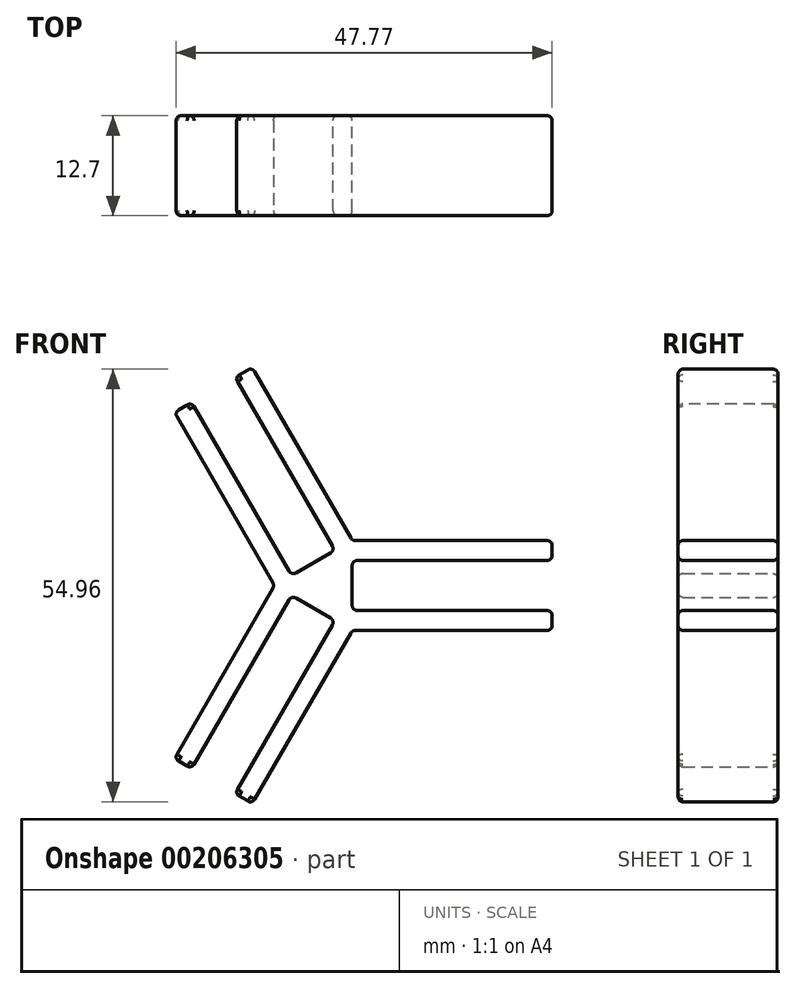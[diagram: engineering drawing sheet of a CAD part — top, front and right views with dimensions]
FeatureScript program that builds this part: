
annotation { "Feature Type Name" : "Feature", "Feature Type Description" : "" }
export const myFeature = defineFeature(function(context is Context, id is Id, definition is map)
    precondition{}
    {
        {
            var Q0;
            Q0=qCreatedBy(makeId("Front.planeOp"),FACE);
            var sketch = newSketch(context, id + "F0", { "sketchPlane" : qUnion([Q0])});
            skLineSegment(sketch, "E0.1", {"start": v(28.7, 3.17) * mm, "end": v(3.93, 3.17) * mm});
            skLineSegment(sketch, "E0.4", {"start": v(3.93, -3.18) * mm, "end": v(28.7, -3.18) * mm});
            skLineSegment(sketch, "E1", {"start": v(-9.4, 27.71) * mm, "end": v(3.3, 5.71) * mm});
            skLineSegment(sketch, "E2", {"start": v(3.3, 5.71) * mm, "end": v(28.7, 5.71) * mm});
            skLineSegment(sketch, "E3", {"start": v(28.7, -5.72) * mm, "end": v(3.3, -5.72) * mm});
            skLineSegment(sketch, "E4", {"start": v(3.3, -5.72) * mm, "end": v(-9.4, -27.71) * mm});
            skLineSegment(sketch, "E5", {"start": v(-19.3, -22) * mm, "end": v(-6.6, 0) * mm});
            skLineSegment(sketch, "E6", {"start": v(-6.6, 0) * mm, "end": v(-19.3, 22) * mm});
            skLineSegment(sketch, "E7", {"start": v(28.7, 3.17) * mm, "end": v(28.7, 5.71) * mm});
            skLineSegment(sketch, "E8", {"start": v(28.7, -5.72) * mm, "end": v(28.7, -3.18) * mm});
            skLineSegment(sketch, "E9", {"start": v(-17.1, -23.27) * mm, "end": v(-19.3, -22) * mm});
            skLineSegment(sketch, "E10", {"start": v(-9.4, -27.71) * mm, "end": v(-11.6, -26.44) * mm});
            skLineSegment(sketch, "E11", {"start": v(-17.1, 23.27) * mm, "end": v(-19.3, 22) * mm});
            skLineSegment(sketch, "E12", {"start": v(3.3, 2.54) * mm, "end": v(3.3, -2.54) * mm});
            skPoint(sketch, "E13.visualSharp", {"position": v(1.83, 3.17) * mm});
            skArc(sketch, "E13.filletArc", {"start": v(3.93, 3.17) * mm, "mid": v(3.49, 2.99) * mm, "end": v(3.3, 2.54) * mm});
            skPoint(sketch, "E14.visualSharp", {"position": v(-3.67, 0) * mm});
            skPoint(sketch, "E15.visualSharp", {"position": v(1.83, -3.18) * mm});
            skArc(sketch, "E16.filletArc", {"start": v(3.3, -2.54) * mm, "mid": v(3.49, -2.99) * mm, "end": v(3.93, -3.18) * mm});
            skLineSegment(sketch, "E17.1.0", {"start": v(0.78, 5) * mm, "end": v(-11.6, 26.44) * mm});
            skLineSegment(sketch, "E17.1.1", {"start": v(-3.85, 1.59) * mm, "end": v(0.55, 4.13) * mm});
            skLineSegment(sketch, "E17.1.2", {"start": v(-17.1, 23.27) * mm, "end": v(-4.72, 1.82) * mm});
            skArc(sketch, "E17.1.3", {"start": v(-4.72, 1.82) * mm, "mid": v(-4.33, 1.52) * mm, "end": v(-3.85, 1.59) * mm});
            skArc(sketch, "E17.1.4", {"start": v(0.55, 4.13) * mm, "mid": v(0.85, 4.51) * mm, "end": v(0.78, 5) * mm});
            skLineSegment(sketch, "E17.2.0", {"start": v(-4.72, -1.82) * mm, "end": v(-17.1, -23.27) * mm});
            skLineSegment(sketch, "E17.2.1", {"start": v(0.55, -4.13) * mm, "end": v(-3.85, -1.59) * mm});
            skLineSegment(sketch, "E17.2.2", {"start": v(-11.6, -26.44) * mm, "end": v(0.78, -5) * mm});
            skArc(sketch, "E17.2.3", {"start": v(0.78, -5) * mm, "mid": v(0.85, -4.51) * mm, "end": v(0.55, -4.13) * mm});
            skArc(sketch, "E17.2.4", {"start": v(-3.85, -1.59) * mm, "mid": v(-4.33, -1.52) * mm, "end": v(-4.72, -1.82) * mm});
            skPoint(sketch, "E17.center", {"position": v(0, 0) * mm});
            skLineSegment(sketch, "E18", {"start": v(-11.6, 26.44) * mm, "end": v(-9.4, 27.71) * mm});
            skSolve(sketch);
        }
        {
            var Q0;
            Q0=makeQuery(id+"F0.imprint","IMPRINT",FACE,{"disambiguationData":[TD([[makeQuery(id+"F0.imprint","IMPRINT",EDGE,{"derivedFrom":sQuery(id+"F0.wireOp",EDGE,"E0.1")}),-1.0]])]});
            extrude(context, id + "F1", {"entities" : qUnion([Q0]), "depth" : 12.7 * mm});
        }
        {
            var Q0;
            Q0=makeQuery(id+"F1.opExtrude","SWEPT_FACE",FACE,{"disambiguationData":[OSD([sQuery(id+"F0.wireOp",EDGE,"E1")])]});
            var Q1;
            Q1=makeQuery(id+"F1.opExtrude","CAP_FACE",FACE,{"disambiguationData":[OSD([sQuery(id+"F0.wireOp",EDGE,"E0.1"),sQuery(id+"F0.wireOp",EDGE,"E0.4"),sQuery(id+"F0.wireOp",EDGE,"E1"),sQuery(id+"F0.wireOp",EDGE,"E2"),sQuery(id+"F0.wireOp",EDGE,"E3"),sQuery(id+"F0.wireOp",EDGE,"E4"),sQuery(id+"F0.wireOp",EDGE,"E5"),sQuery(id+"F0.wireOp",EDGE,"E6"),sQuery(id+"F0.wireOp",EDGE,"E7"),sQuery(id+"F0.wireOp",EDGE,"E8"),sQuery(id+"F0.wireOp",EDGE,"E9"),sQuery(id+"F0.wireOp",EDGE,"E10"),sQuery(id+"F0.wireOp",EDGE,"E11"),sQuery(id+"F0.wireOp",EDGE,"E12"),sQuery(id+"F0.wireOp",EDGE,"E13.filletArc"),sQuery(id+"F0.wireOp",EDGE,"E16.filletArc"),sQuery(id+"F0.wireOp",EDGE,"E17.1.0"),sQuery(id+"F0.wireOp",EDGE,"E17.1.1"),sQuery(id+"F0.wireOp",EDGE,"E17.1.2"),sQuery(id+"F0.wireOp",EDGE,"E17.1.3"),sQuery(id+"F0.wireOp",EDGE,"E17.1.4"),sQuery(id+"F0.wireOp",EDGE,"E17.2.0"),sQuery(id+"F0.wireOp",EDGE,"E17.2.1"),sQuery(id+"F0.wireOp",EDGE,"E17.2.2"),sQuery(id+"F0.wireOp",EDGE,"E17.2.3"),sQuery(id+"F0.wireOp",EDGE,"E17.2.4"),sQuery(id+"F0.wireOp",EDGE,"E18")])],"isStart":false});
            var Q2;
            Q2=makeQuery(id+"F1.opExtrude","CAP_FACE",FACE,{"disambiguationData":[OSD([sQuery(id+"F0.wireOp",EDGE,"E0.1"),sQuery(id+"F0.wireOp",EDGE,"E0.4"),sQuery(id+"F0.wireOp",EDGE,"E1"),sQuery(id+"F0.wireOp",EDGE,"E2"),sQuery(id+"F0.wireOp",EDGE,"E3"),sQuery(id+"F0.wireOp",EDGE,"E4"),sQuery(id+"F0.wireOp",EDGE,"E5"),sQuery(id+"F0.wireOp",EDGE,"E6"),sQuery(id+"F0.wireOp",EDGE,"E7"),sQuery(id+"F0.wireOp",EDGE,"E8"),sQuery(id+"F0.wireOp",EDGE,"E9"),sQuery(id+"F0.wireOp",EDGE,"E10"),sQuery(id+"F0.wireOp",EDGE,"E11"),sQuery(id+"F0.wireOp",EDGE,"E12"),sQuery(id+"F0.wireOp",EDGE,"E13.filletArc"),sQuery(id+"F0.wireOp",EDGE,"E16.filletArc"),sQuery(id+"F0.wireOp",EDGE,"E17.1.0"),sQuery(id+"F0.wireOp",EDGE,"E17.1.1"),sQuery(id+"F0.wireOp",EDGE,"E17.1.2"),sQuery(id+"F0.wireOp",EDGE,"E17.1.3"),sQuery(id+"F0.wireOp",EDGE,"E17.1.4"),sQuery(id+"F0.wireOp",EDGE,"E17.2.0"),sQuery(id+"F0.wireOp",EDGE,"E17.2.1"),sQuery(id+"F0.wireOp",EDGE,"E17.2.2"),sQuery(id+"F0.wireOp",EDGE,"E17.2.3"),sQuery(id+"F0.wireOp",EDGE,"E17.2.4"),sQuery(id+"F0.wireOp",EDGE,"E18")])],"isStart":true});
            var Q3;
            Q3=makeQuery(id+"F1.opExtrude","SWEPT_FACE",FACE,{"disambiguationData":[OSD([sQuery(id+"F0.wireOp",EDGE,"E6")])]});
            var Q4;
            Q4=makeQuery(id+"F1.opExtrude","SWEPT_FACE",FACE,{"disambiguationData":[OSD([sQuery(id+"F0.wireOp",EDGE,"E3")])]});
            fillet(context, id + "F2", {"entities" : qUnion([Q0, Q1, Q2, Q3, Q4]), "radius" : 0.64 * mm, "tangentPropagation" : true, "allowEdgeOverflow" : false});
        }
        {
            var Q0;
            Q0=makeQuery(id+"F1.opExtrude","SWEPT_FACE",FACE,{"disambiguationData":[OSD([sQuery(id+"F0.wireOp",EDGE,"E8")])]});
            var Q1;
            Q1=makeQuery(id+"F1.opExtrude","SWEPT_FACE",FACE,{"disambiguationData":[OSD([sQuery(id+"F0.wireOp",EDGE,"E7")])]});
            var Q2;
            Q2=makeQuery(id+"F1.opExtrude","SWEPT_FACE",FACE,{"disambiguationData":[OSD([sQuery(id+"F0.wireOp",EDGE,"E10")])]});
            var Q3;
            Q3=makeQuery(id+"F1.opExtrude","SWEPT_FACE",FACE,{"disambiguationData":[OSD([sQuery(id+"F0.wireOp",EDGE,"E9")])]});
            var Q4;
            Q4=makeQuery(id+"F1.opExtrude","SWEPT_FACE",FACE,{"disambiguationData":[OSD([sQuery(id+"F0.wireOp",EDGE,"E18")])]});
            var Q5;
            Q5=makeQuery(id+"F1.opExtrude","SWEPT_FACE",FACE,{"disambiguationData":[OSD([sQuery(id+"F0.wireOp",EDGE,"E11")])]});
            fillet(context, id + "F3", {"entities" : qUnion([Q0, Q1, Q2, Q3, Q4, Q5]), "radius" : 0.64 * mm, "tangentPropagation" : true, "allowEdgeOverflow" : false});
        }
    });
